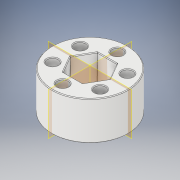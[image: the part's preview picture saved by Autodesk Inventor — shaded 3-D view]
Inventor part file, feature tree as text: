
AUTODESK INVENTOR PART (.ipt)
format: ipt  version: 2017.1 (Build 211199000, 199)  size: 276,480 bytes
history: native  units: in
note: dims shown in document units (in); Inventor stores cm internally (conversion verified against a paired STEP export)
features: plane x1, other x1, fillet x1
ambient origin geometry x8: Origin, YZ Plane, XZ Plane, XY Plane, X Axis, Y Axis, Z Axis, Center Point
bodies: Solid1 (feature_tree)
feature tree (3):
  plane  "Work Plane1"
  other  "Work Axis1"
  fillet  "Fillet2"  Radius=0.6184in
